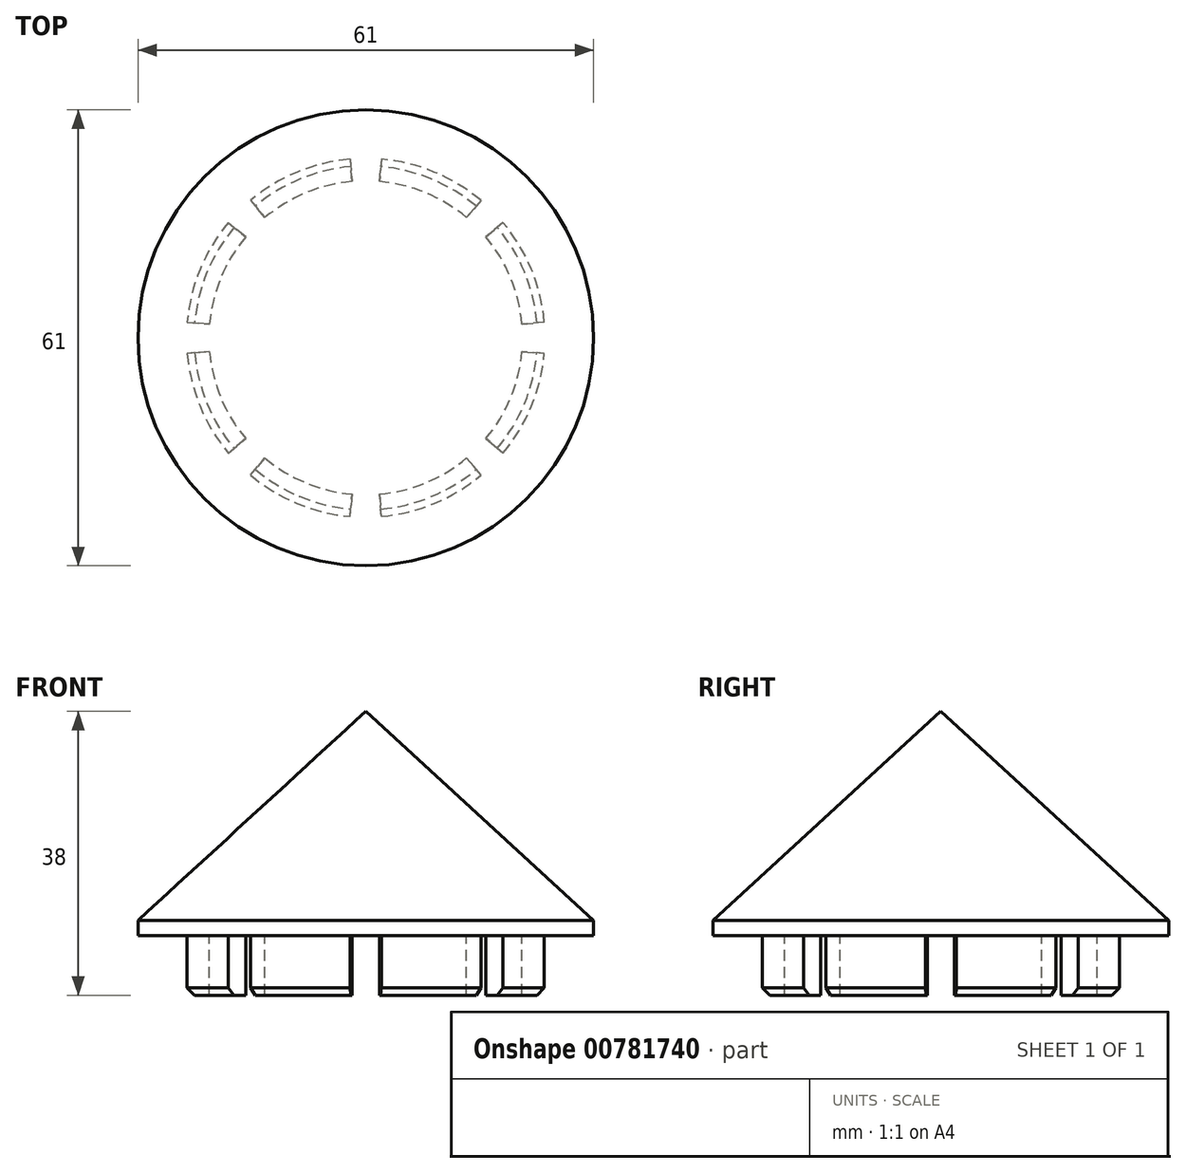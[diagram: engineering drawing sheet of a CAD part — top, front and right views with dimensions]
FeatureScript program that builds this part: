
annotation { "Feature Type Name" : "Feature", "Feature Type Description" : "" }
export const myFeature = defineFeature(function(context is Context, id is Id, definition is map)
    precondition{}
    {
        {
            assignVariable(context, id + "F0", {"name" : "td", "anyValue" : 8});
        }
        {
            assignVariable(context, id + "F1", {"name" : "S", "anyValue" : 2});
        }
        {
            var Q0;
            Q0=qCreatedBy(makeId("Front.planeOp"),FACE);
            var sketch = newSketch(context, id + "F2", { "sketchPlane" : qUnion([Q0])});
            skLineSegment(sketch, "E0", {"start": v(-30.5, 0) * mm, "end": v(0, 0) * mm});
            skLineSegment(sketch, "E1", {"start": v(0, 71.38) * mm, "end": v(0, -63.34) * mm, "construction": true});
            skLineSegment(sketch, "E2", {"start": v(0, 30) * mm, "end": v(0, 0) * mm});
            skLineSegment(sketch, "E3", {"start": v(-30.5, 0) * mm, "end": v(-30.5, 2) * mm});
            skLineSegment(sketch, "E4", {"start": v(-30.5, 2) * mm, "end": v(0, 30) * mm});
            skSolve(sketch);
        }
        {
            var Q0;
            Q0=makeQuery(id+"F2.imprint","IMPRINT",FACE,{"disambiguationData":[TD([[makeQuery(id+"F2.imprint","IMPRINT",EDGE,{"derivedFrom":sQuery(id+"F2.wireOp",EDGE,"E0")}),1.0]])]});
            var Q1;
            Q1=sQuery(id+"F2.wireOp",EDGE,"E1");
            var Q2;
            Q2=sQuery(id+"F2.wireOp",EDGE,"QkWRGxjC-w0jD-TnS2-GxZ8-BeYZWvhwOgx8");
            var Q3;
            Q3=sQuery(id+"F2.wireOp",EDGE,"E0");
            var Q4;
            Q4=sQuery(id+"F2.wireOp",EDGE,"E1");
            revolve(context, id + "F3", {"surfaceOperationType" : NewSurfaceOperationType.NEW, "entities" : qUnion([Q0]), "surfaceEntities" : qUnion([Q1, Q2, Q3]), "axis" : qUnion([Q4]), "revolveType" : RevolveType.FULL});
        }
        {
            var Q0;
            Q0=makeQuery(id+"F3.opRevolve","SWEPT_FACE",FACE,{"disambiguationData":[OSD([sQuery(id+"F2.wireOp",EDGE,"E0")])]});
            var sketch = newSketch(context, id + "F4", { "sketchPlane" : qUnion([Q0])});
            skCircle(sketch, "E5", {"center": v(0, 0) * mm, "radius": 24 * mm});
            skCircle(sketch, "E6", {"center": v(0, 0) * mm, "radius": 21 * mm});
            skLineSegment(sketch, "E7", {"start": v(0, 0) * mm, "end": v(0, -30.5) * mm, "construction": true});
            skLineSegment(sketch, "E8", {"start": v(0, 0) * mm, "end": v(-2.66, -30.38) * mm, "construction": true});
            skLineSegment(sketch, "E9", {"start": v(0, 0) * mm, "end": v(2.66, -30.38) * mm, "construction": true});
            skLineSegment(sketch, "E10", {"start": v(-2.66, -30.38) * mm, "end": v(-1.83, -20.92) * mm});
            skLineSegment(sketch, "E11", {"start": v(1.83, -20.92) * mm, "end": v(2.66, -30.38) * mm});
            skPoint(sketch, "E12.center", {"position": v(0.17, 2) * mm});
            skLineSegment(sketch, "E12.anchor1", {"start": v(0.17, 2) * mm, "end": v(-2.66, -30.38) * mm, "construction": true});
            skLineSegment(sketch, "E12.anchor2", {"start": v(0.17, 2) * mm, "end": v(-1.92, -21.92) * mm, "construction": true});
            skLineSegment(sketch, "E13", {"start": v(-1.83, -20.92) * mm, "end": v(-2.66, -30.38) * mm});
            skLineSegment(sketch, "E14.1.0", {"start": v(19.6, -23.36) * mm, "end": v(13.5, -16.09) * mm});
            skLineSegment(sketch, "E14.1.1", {"start": v(16.09, -13.5) * mm, "end": v(23.36, -19.6) * mm});
            skLineSegment(sketch, "E14.1.2", {"start": v(16.09, -13.5) * mm, "end": v(23.36, -19.6) * mm});
            skLineSegment(sketch, "E14.1.3", {"start": v(13.5, -16.09) * mm, "end": v(19.6, -23.36) * mm});
            skLineSegment(sketch, "E14.2.0", {"start": v(30.38, -2.66) * mm, "end": v(20.92, -1.83) * mm});
            skLineSegment(sketch, "E14.2.1", {"start": v(20.92, 1.83) * mm, "end": v(30.38, 2.66) * mm});
            skLineSegment(sketch, "E14.2.2", {"start": v(20.92, 1.83) * mm, "end": v(30.38, 2.66) * mm});
            skLineSegment(sketch, "E14.2.3", {"start": v(20.92, -1.83) * mm, "end": v(30.38, -2.66) * mm});
            skLineSegment(sketch, "E14.3.0", {"start": v(23.36, 19.6) * mm, "end": v(16.09, 13.5) * mm});
            skLineSegment(sketch, "E14.3.1", {"start": v(13.5, 16.09) * mm, "end": v(19.6, 23.36) * mm});
            skLineSegment(sketch, "E14.3.2", {"start": v(13.5, 16.09) * mm, "end": v(19.6, 23.36) * mm});
            skLineSegment(sketch, "E14.3.3", {"start": v(16.09, 13.5) * mm, "end": v(23.36, 19.6) * mm});
            skLineSegment(sketch, "E14.4.0", {"start": v(2.66, 30.38) * mm, "end": v(1.83, 20.92) * mm});
            skLineSegment(sketch, "E14.4.1", {"start": v(-1.83, 20.92) * mm, "end": v(-2.66, 30.38) * mm});
            skLineSegment(sketch, "E14.4.2", {"start": v(-1.83, 20.92) * mm, "end": v(-2.66, 30.38) * mm});
            skLineSegment(sketch, "E14.4.3", {"start": v(1.83, 20.92) * mm, "end": v(2.66, 30.38) * mm});
            skLineSegment(sketch, "E14.5.0", {"start": v(-19.6, 23.36) * mm, "end": v(-13.5, 16.09) * mm});
            skLineSegment(sketch, "E14.5.1", {"start": v(-16.09, 13.5) * mm, "end": v(-23.36, 19.6) * mm});
            skLineSegment(sketch, "E14.5.2", {"start": v(-16.09, 13.5) * mm, "end": v(-23.36, 19.6) * mm});
            skLineSegment(sketch, "E14.5.3", {"start": v(-13.5, 16.09) * mm, "end": v(-19.6, 23.36) * mm});
            skLineSegment(sketch, "E14.6.0", {"start": v(-30.38, 2.66) * mm, "end": v(-20.92, 1.83) * mm});
            skLineSegment(sketch, "E14.6.1", {"start": v(-20.92, -1.83) * mm, "end": v(-30.38, -2.66) * mm});
            skLineSegment(sketch, "E14.6.2", {"start": v(-20.92, -1.83) * mm, "end": v(-30.38, -2.66) * mm});
            skLineSegment(sketch, "E14.6.3", {"start": v(-20.92, 1.83) * mm, "end": v(-30.38, 2.66) * mm});
            skLineSegment(sketch, "E14.7.0", {"start": v(-23.36, -19.6) * mm, "end": v(-16.09, -13.5) * mm});
            skLineSegment(sketch, "E14.7.1", {"start": v(-13.5, -16.09) * mm, "end": v(-19.6, -23.36) * mm});
            skLineSegment(sketch, "E14.7.2", {"start": v(-13.5, -16.09) * mm, "end": v(-19.6, -23.36) * mm});
            skLineSegment(sketch, "E14.7.3", {"start": v(-16.09, -13.5) * mm, "end": v(-23.36, -19.6) * mm});
            skSolve(sketch);
        }
        {
            var Q0;
            {var subQ0=sQuery(id+"F4.wireOp",EDGE,"E14.4.3");var subQ1=sQuery(id+"F4.wireOp",EDGE,"E5");var subQ2=makeQuery(id+"F4.imprint","INTERSECT",VERTEX,{"derivedFrom":[subQ1,subQ0]});Q0=makeQuery(id+"F4.imprint","IMPRINT",FACE,{"disambiguationData":[TD([[makeQuery(id+"F4.imprint","IMPRINT",EDGE,{"disambiguationData":[TD([[subQ2,-1.0]])],"derivedFrom":subQ1}),1.0]])]});}
            var Q1;
            {var subQ0=sQuery(id+"F4.wireOp",EDGE,"E14.3.2");var subQ1=sQuery(id+"F4.wireOp",EDGE,"E5");var subQ2=makeQuery(id+"F4.imprint","INTERSECT",VERTEX,{"derivedFrom":[subQ1,subQ0]});Q1=makeQuery(id+"F4.imprint","IMPRINT",FACE,{"disambiguationData":[TD([[makeQuery(id+"F4.imprint","IMPRINT",EDGE,{"disambiguationData":[TD([[subQ2,-1.0]])],"derivedFrom":subQ1}),1.0]])]});}
            var Q2;
            {var subQ0=sQuery(id+"F4.wireOp",EDGE,"E14.3.3");var subQ1=sQuery(id+"F4.wireOp",EDGE,"E5");var subQ2=makeQuery(id+"F4.imprint","INTERSECT",VERTEX,{"derivedFrom":[subQ1,subQ0]});Q2=makeQuery(id+"F4.imprint","IMPRINT",FACE,{"disambiguationData":[TD([[makeQuery(id+"F4.imprint","IMPRINT",EDGE,{"disambiguationData":[TD([[subQ2,-1.0]])],"derivedFrom":subQ1}),1.0]])]});}
            var Q3;
            {var subQ0=sQuery(id+"F4.wireOp",EDGE,"E14.3.3");var subQ1=sQuery(id+"F4.wireOp",EDGE,"E5");var subQ2=makeQuery(id+"F4.imprint","INTERSECT",VERTEX,{"derivedFrom":[subQ1,subQ0]});Q3=makeQuery(id+"F4.imprint","IMPRINT",FACE,{"disambiguationData":[TD([[makeQuery(id+"F4.imprint","IMPRINT",EDGE,{"disambiguationData":[TD([[subQ2,1.0]])],"derivedFrom":subQ1}),1.0]])]});}
            var Q4;
            {var subQ0=sQuery(id+"F4.wireOp",EDGE,"E14.2.2");var subQ1=sQuery(id+"F4.wireOp",EDGE,"E5");var subQ2=makeQuery(id+"F4.imprint","INTERSECT",VERTEX,{"derivedFrom":[subQ1,subQ0]});Q4=makeQuery(id+"F4.imprint","IMPRINT",FACE,{"disambiguationData":[TD([[makeQuery(id+"F4.imprint","IMPRINT",EDGE,{"disambiguationData":[TD([[subQ2,1.0]])],"derivedFrom":subQ1}),1.0]])]});}
            var Q5;
            {var subQ0=sQuery(id+"F4.wireOp",EDGE,"E14.1.2");var subQ1=sQuery(id+"F4.wireOp",EDGE,"E5");var subQ2=makeQuery(id+"F4.imprint","INTERSECT",VERTEX,{"derivedFrom":[subQ1,subQ0]});Q5=makeQuery(id+"F4.imprint","IMPRINT",FACE,{"disambiguationData":[TD([[makeQuery(id+"F4.imprint","IMPRINT",EDGE,{"disambiguationData":[TD([[subQ2,-1.0]])],"derivedFrom":subQ1}),1.0]])]});}
            var Q6;
            {var subQ0=sQuery(id+"F4.wireOp",EDGE,"E14.1.3");var subQ1=sQuery(id+"F4.wireOp",EDGE,"E5");var subQ2=makeQuery(id+"F4.imprint","INTERSECT",VERTEX,{"derivedFrom":[subQ1,subQ0]});Q6=makeQuery(id+"F4.imprint","IMPRINT",FACE,{"disambiguationData":[TD([[makeQuery(id+"F4.imprint","IMPRINT",EDGE,{"disambiguationData":[TD([[subQ2,-1.0]])],"derivedFrom":subQ1}),1.0]])]});}
            var Q7;
            {var subQ0=sQuery(id+"F4.wireOp",EDGE,"E11");var subQ1=sQuery(id+"F4.wireOp",EDGE,"E5");var subQ2=makeQuery(id+"F4.imprint","INTERSECT",VERTEX,{"derivedFrom":[subQ1,subQ0]});Q7=makeQuery(id+"F4.imprint","IMPRINT",FACE,{"disambiguationData":[TD([[makeQuery(id+"F4.imprint","IMPRINT",EDGE,{"disambiguationData":[TD([[subQ2,-1.0]])],"derivedFrom":subQ1}),1.0]])]});}
            var Q8;
            {var subQ0=sQuery(id+"F4.wireOp",EDGE,"E13");var subQ1=sQuery(id+"F4.wireOp",EDGE,"E5");var subQ2=makeQuery(id+"F4.imprint","INTERSECT",VERTEX,{"derivedFrom":[subQ1,subQ0]});Q8=makeQuery(id+"F4.imprint","IMPRINT",FACE,{"disambiguationData":[TD([[makeQuery(id+"F4.imprint","IMPRINT",EDGE,{"disambiguationData":[TD([[subQ2,-1.0]])],"derivedFrom":subQ1}),1.0]])]});}
            var Q9;
            {var subQ0=sQuery(id+"F4.wireOp",EDGE,"E14.7.2");var subQ1=sQuery(id+"F4.wireOp",EDGE,"E5");var subQ2=makeQuery(id+"F4.imprint","INTERSECT",VERTEX,{"derivedFrom":[subQ1,subQ0]});Q9=makeQuery(id+"F4.imprint","IMPRINT",FACE,{"disambiguationData":[TD([[makeQuery(id+"F4.imprint","IMPRINT",EDGE,{"disambiguationData":[TD([[subQ2,-1.0]])],"derivedFrom":subQ1}),1.0]])]});}
            var Q10;
            {var subQ0=sQuery(id+"F4.wireOp",EDGE,"E14.7.3");var subQ1=sQuery(id+"F4.wireOp",EDGE,"E5");var subQ2=makeQuery(id+"F4.imprint","INTERSECT",VERTEX,{"derivedFrom":[subQ1,subQ0]});Q10=makeQuery(id+"F4.imprint","IMPRINT",FACE,{"disambiguationData":[TD([[makeQuery(id+"F4.imprint","IMPRINT",EDGE,{"disambiguationData":[TD([[subQ2,-1.0]])],"derivedFrom":subQ1}),1.0]])]});}
            var Q11;
            {var subQ0=sQuery(id+"F4.wireOp",EDGE,"E14.6.2");var subQ1=sQuery(id+"F4.wireOp",EDGE,"E5");var subQ2=makeQuery(id+"F4.imprint","INTERSECT",VERTEX,{"derivedFrom":[subQ1,subQ0]});Q11=makeQuery(id+"F4.imprint","IMPRINT",FACE,{"disambiguationData":[TD([[makeQuery(id+"F4.imprint","IMPRINT",EDGE,{"disambiguationData":[TD([[subQ2,-1.0]])],"derivedFrom":subQ1}),1.0]])]});}
            var Q12;
            {var subQ0=sQuery(id+"F4.wireOp",EDGE,"E14.6.3");var subQ1=sQuery(id+"F4.wireOp",EDGE,"E5");var subQ2=makeQuery(id+"F4.imprint","INTERSECT",VERTEX,{"derivedFrom":[subQ1,subQ0]});Q12=makeQuery(id+"F4.imprint","IMPRINT",FACE,{"disambiguationData":[TD([[makeQuery(id+"F4.imprint","IMPRINT",EDGE,{"disambiguationData":[TD([[subQ2,-1.0]])],"derivedFrom":subQ1}),1.0]])]});}
            var Q13;
            {var subQ0=sQuery(id+"F4.wireOp",EDGE,"E14.5.2");var subQ1=sQuery(id+"F4.wireOp",EDGE,"E5");var subQ2=makeQuery(id+"F4.imprint","INTERSECT",VERTEX,{"derivedFrom":[subQ1,subQ0]});Q13=makeQuery(id+"F4.imprint","IMPRINT",FACE,{"disambiguationData":[TD([[makeQuery(id+"F4.imprint","IMPRINT",EDGE,{"disambiguationData":[TD([[subQ2,-1.0]])],"derivedFrom":subQ1}),1.0]])]});}
            var Q14;
            {var subQ0=sQuery(id+"F4.wireOp",EDGE,"E14.5.3");var subQ1=sQuery(id+"F4.wireOp",EDGE,"E5");var subQ2=makeQuery(id+"F4.imprint","INTERSECT",VERTEX,{"derivedFrom":[subQ1,subQ0]});Q14=makeQuery(id+"F4.imprint","IMPRINT",FACE,{"disambiguationData":[TD([[makeQuery(id+"F4.imprint","IMPRINT",EDGE,{"disambiguationData":[TD([[subQ2,-1.0]])],"derivedFrom":subQ1}),1.0]])]});}
            var Q15;
            {var subQ0=sQuery(id+"F4.wireOp",EDGE,"E14.4.2");var subQ1=sQuery(id+"F4.wireOp",EDGE,"E5");var subQ2=makeQuery(id+"F4.imprint","INTERSECT",VERTEX,{"derivedFrom":[subQ1,subQ0]});Q15=makeQuery(id+"F4.imprint","IMPRINT",FACE,{"disambiguationData":[TD([[makeQuery(id+"F4.imprint","IMPRINT",EDGE,{"disambiguationData":[TD([[subQ2,-1.0]])],"derivedFrom":subQ1}),1.0]])]});}
            extrude(context, id + "F5", {"entities" : qUnion([Q0, Q1, Q2, Q3, Q4, Q5, Q6, Q7, Q8, Q9, Q10, Q11, Q12, Q13, Q14, Q15]), "operationType" : NewBodyOperationType.ADD, "depth" : (getVariable(context, 'td')) * mm, "offsetDistance" : 25 * mm});
        }
        {
            var Q0;
            Q0=makeQuery(id+"F5.opExtrude","CAP_EDGE",EDGE,{"disambiguationData":[OSD([sQuery(id+"F4.wireOp",EDGE,"E5")])],"isStart":false});
            chamfer(context, id + "F6", {"entities" : qUnion([Q0]), "width" : 1 * mm, "tangentPropagation" : true});
        }
        {
            var Q0;
            Q0=qCreatedBy(makeId("Right.planeOp"),FACE);
            var sketch = newSketch(context, id + "F7", { "sketchPlane" : qUnion([Q0])});
            skLineSegment(sketch, "E15", {"start": v(24, 0) * mm, "end": v(24, -7) * mm});
            skLineSegment(sketch, "E16", {"start": v(24, -2) * mm, "end": v(25, -2) * mm});
            skLineSegment(sketch, "E17", {"start": v(25, -2) * mm, "end": v(24, -5) * mm});
            skLineSegment(sketch, "E18", {"start": v(24, -5) * mm, "end": v(24, -2) * mm});
            skSolve(sketch);
        }
        {
            var Q0;
            Q0=makeQuery(id+"F7.imprint","IMPRINT",FACE,{"disambiguationData":[TD([[makeQuery(id+"F7.imprint","IMPRINT",EDGE,{"derivedFrom":sQuery(id+"F7.wireOp",EDGE,"E16")}),-1.0]])]});
            var Q1;
            Q1=sQuery(id+"F2.wireOp",EDGE,"E1");
            revolve(context, id + "F8", {"operationType" : NewBodyOperationType.ADD, "surfaceOperationType" : NewSurfaceOperationType.NEW, "entities" : qUnion([Q0]), "axis" : qUnion([Q1]), "revolveType" : RevolveType.FULL});
        }
        {
            var Q0;
            Q0=qCreatedBy(makeId("Top.planeOp"),FACE);
            var sketch = newSketch(context, id + "F9", { "sketchPlane" : qUnion([Q0])});
            skPoint(sketch, "E19.0", {"position": v(23.36, 19.6) * mm});
            skPoint(sketch, "E20.0", {"position": v(19.6, 23.36) * mm});
            skPoint(sketch, "E21.0", {"position": v(30.38, 2.66) * mm});
            skPoint(sketch, "E22.0", {"position": v(30.38, -2.66) * mm});
            skPoint(sketch, "E23.0", {"position": v(23.36, -19.6) * mm});
            skPoint(sketch, "E24.0", {"position": v(19.6, -23.36) * mm});
            skPoint(sketch, "E25.0", {"position": v(2.66, -30.38) * mm});
            skPoint(sketch, "E26.0", {"position": v(-2.66, -30.38) * mm});
            skPoint(sketch, "E27.0", {"position": v(-19.6, -23.36) * mm});
            skPoint(sketch, "E28.0", {"position": v(-23.36, -19.6) * mm});
            skPoint(sketch, "E29.0", {"position": v(-30.38, -2.66) * mm});
            skPoint(sketch, "E30.0", {"position": v(-30.38, 2.66) * mm});
            skPoint(sketch, "E31.0", {"position": v(-23.36, 19.6) * mm});
            skPoint(sketch, "E32.0", {"position": v(-19.6, 23.36) * mm});
            skPoint(sketch, "E33.0", {"position": v(-2.66, 30.38) * mm});
            skPoint(sketch, "E34.0", {"position": v(2.66, 30.38) * mm});
            skLineSegment(sketch, "E35", {"start": v(-30.38, 2.66) * mm, "end": v(0, 0) * mm});
            skLineSegment(sketch, "E36", {"start": v(0, 0) * mm, "end": v(-30.38, -2.66) * mm});
            skLineSegment(sketch, "E37", {"start": v(-23.36, -19.6) * mm, "end": v(0, 0) * mm});
            skLineSegment(sketch, "E38", {"start": v(-19.6, -23.36) * mm, "end": v(0, 0) * mm});
            skLineSegment(sketch, "E39", {"start": v(-2.66, -30.38) * mm, "end": v(0, 0) * mm});
            skLineSegment(sketch, "E40", {"start": v(2.66, -30.38) * mm, "end": v(0, 0) * mm});
            skLineSegment(sketch, "E41", {"start": v(19.6, -23.36) * mm, "end": v(0, 0) * mm});
            skLineSegment(sketch, "E42", {"start": v(23.36, -19.6) * mm, "end": v(0, 0) * mm});
            skLineSegment(sketch, "E43", {"start": v(30.38, -2.66) * mm, "end": v(0, 0) * mm});
            skLineSegment(sketch, "E44", {"start": v(30.38, 2.66) * mm, "end": v(0, 0) * mm});
            skLineSegment(sketch, "E45", {"start": v(23.36, 19.6) * mm, "end": v(0, 0) * mm});
            skLineSegment(sketch, "E46", {"start": v(19.6, 23.36) * mm, "end": v(0, 0) * mm});
            skLineSegment(sketch, "E47", {"start": v(2.66, 30.38) * mm, "end": v(0, 0) * mm});
            skLineSegment(sketch, "E48", {"start": v(-2.66, 30.38) * mm, "end": v(0, 0) * mm});
            skLineSegment(sketch, "E49", {"start": v(-19.6, 23.36) * mm, "end": v(0, 0) * mm});
            skLineSegment(sketch, "E50", {"start": v(-23.36, 19.6) * mm, "end": v(0, 0) * mm});
            skCircle(sketch, "E51", {"center": v(0, 0) * mm, "radius": 30.5 * mm});
            skSolve(sketch);
        }
        {
            var Q0;
            {var subQ0=sQuery(id+"F9.wireOp",EDGE,"E49");Q0=makeQuery(id+"F9.imprint","IMPRINT",FACE,{"disambiguationData":[TD([[makeQuery(id+"F9.imprint","IMPRINT",EDGE,{"derivedFrom":subQ0}),-1.0]])]});}
            var Q1;
            {var subQ0=sQuery(id+"F9.wireOp",EDGE,"E35");Q1=makeQuery(id+"F9.imprint","IMPRINT",FACE,{"disambiguationData":[TD([[makeQuery(id+"F9.imprint","IMPRINT",EDGE,{"derivedFrom":subQ0}),-1.0]])]});}
            var Q2;
            {var subQ0=sQuery(id+"F9.wireOp",EDGE,"E37");Q2=makeQuery(id+"F9.imprint","IMPRINT",FACE,{"disambiguationData":[TD([[makeQuery(id+"F9.imprint","IMPRINT",EDGE,{"derivedFrom":subQ0}),-1.0]])]});}
            var Q3;
            {var subQ0=sQuery(id+"F4.wireOp",EDGE,"E14.4.3");var subQ1=sQuery(id+"F4.wireOp",EDGE,"E5");var subQ2=makeQuery(id+"F4.imprint","INTERSECT",VERTEX,{"derivedFrom":[subQ1,subQ0]});Q3=makeQuery(id+"F4.imprint","IMPRINT",FACE,{"disambiguationData":[TD([[makeQuery(id+"F4.imprint","IMPRINT",EDGE,{"disambiguationData":[TD([[subQ2,-1.0]])],"derivedFrom":subQ1}),-1.0]])]});}
            var Q4;
            {var subQ0=sQuery(id+"F9.wireOp",EDGE,"E39");Q4=makeQuery(id+"F9.imprint","IMPRINT",FACE,{"disambiguationData":[TD([[makeQuery(id+"F9.imprint","IMPRINT",EDGE,{"derivedFrom":subQ0}),-1.0]])]});}
            var Q5;
            {var subQ0=sQuery(id+"F9.wireOp",EDGE,"E41");Q5=makeQuery(id+"F9.imprint","IMPRINT",FACE,{"disambiguationData":[TD([[makeQuery(id+"F9.imprint","IMPRINT",EDGE,{"derivedFrom":subQ0}),-1.0]])]});}
            var Q6;
            {var subQ0=sQuery(id+"F9.wireOp",EDGE,"E43");Q6=makeQuery(id+"F9.imprint","IMPRINT",FACE,{"disambiguationData":[TD([[makeQuery(id+"F9.imprint","IMPRINT",EDGE,{"derivedFrom":subQ0}),-1.0]])]});}
            var Q7;
            {var subQ0=sQuery(id+"F9.wireOp",EDGE,"E47");Q7=makeQuery(id+"F9.imprint","IMPRINT",FACE,{"disambiguationData":[TD([[makeQuery(id+"F9.imprint","IMPRINT",EDGE,{"derivedFrom":subQ0}),-1.0]])]});}
            var Q8;
            {var subQ0=sQuery(id+"F4.wireOp",EDGE,"E14.1.3");var subQ1=sQuery(id+"F4.wireOp",EDGE,"E5");var subQ2=makeQuery(id+"F4.imprint","INTERSECT",VERTEX,{"derivedFrom":[subQ1,subQ0]});Q8=makeQuery(id+"F4.imprint","IMPRINT",FACE,{"disambiguationData":[TD([[makeQuery(id+"F4.imprint","IMPRINT",EDGE,{"disambiguationData":[TD([[subQ2,-1.0]])],"derivedFrom":subQ1}),-1.0]])]});}
            var Q9;
            {var subQ0=sQuery(id+"F9.wireOp",EDGE,"E45");Q9=makeQuery(id+"F9.imprint","IMPRINT",FACE,{"disambiguationData":[TD([[makeQuery(id+"F9.imprint","IMPRINT",EDGE,{"derivedFrom":subQ0}),-1.0]])]});}
            extrude(context, id + "F10", {"entities" : qUnion([Q0, Q1, Q2, Q3, Q4, Q5, Q6, Q7, Q8, Q9]), "operationType" : NewBodyOperationType.REMOVE, "oppositeDirection" : true, "depth" : 25 * mm, "offsetDistance" : 25 * mm});
        }
        {
            var Q0;
            Q0=qCreatedBy(makeId("Top.planeOp"),FACE);
            cPlane(context, id + "F11", {"entities" : qUnion([Q0]), "cplaneType" : CPlaneType.OFFSET, "offset" : (getVariable(context, 'S')) * mm, "width" : 150 * mm, "height" : 150 * mm});
        }
    });
